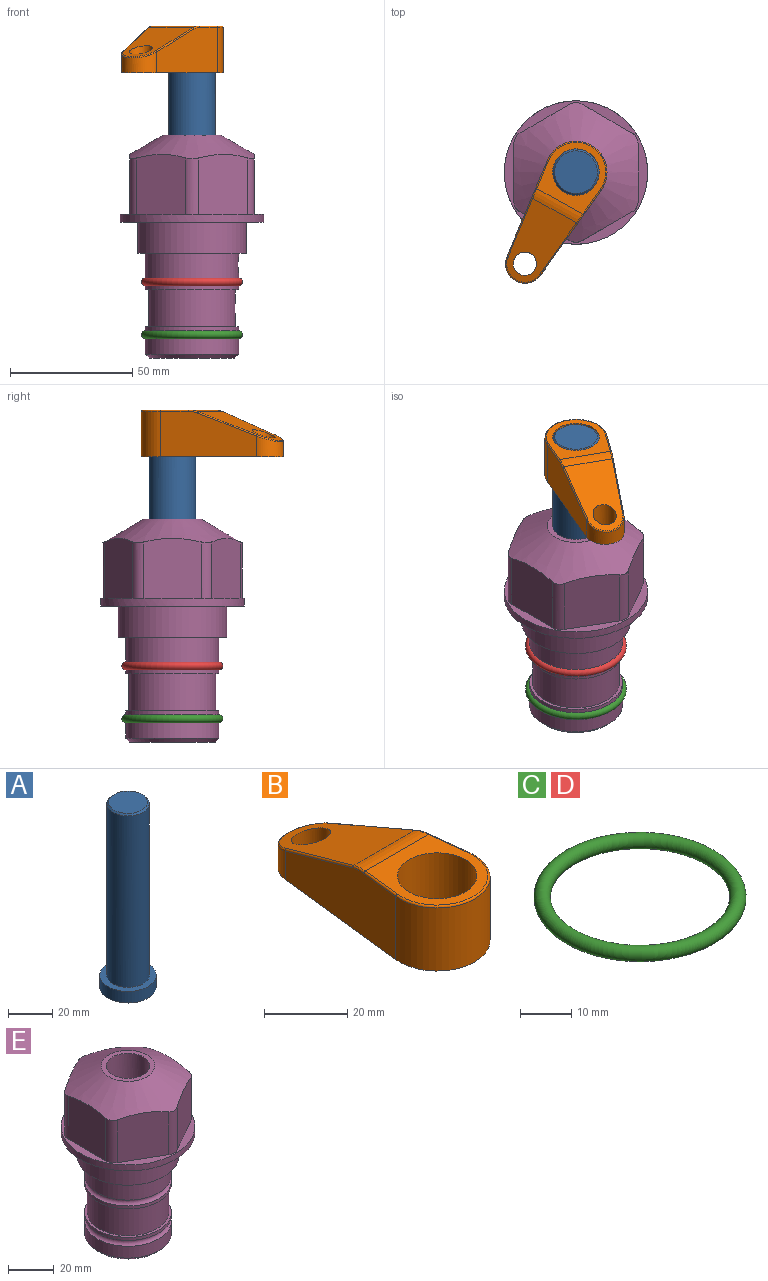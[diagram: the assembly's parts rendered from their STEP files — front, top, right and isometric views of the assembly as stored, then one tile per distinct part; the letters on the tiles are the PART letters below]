
ASSEMBLY  parts=5 mates=3
PART A: 6 faces, bbox 25.4x25.4x101.6 mm
  f0: plane 17.46x17.46mm, normal (0,0,1), area 239.5mm2, adj f5
  f1: plane 25.4x25.4mm, normal (0,0,-1), area 506.7mm2, adj f2
  f2: cylinder r=12.7mm len=25.4mm, axis (0,0,1), area 506.7mm2, adj f1,f3
  f3: plane 25.4x25.4mm, normal (0,0,1), area 221.7mm2, adj f2,f4
  f4: cylinder r=9.53mm len=94.46mm, axis (0,0,1), area 5653mm2, adj f3,f5
  f5: cone r=8.73mm half-angle=45deg, axis (0,0,-1), area 64.4mm2, adj f0,f4
PART B: 44 faces, bbox 27.5x64.5x19.1 mm
  f0: plane 2.3x0.95mm, normal (0,0,-1), area 1mm2, adj f25,f30,f34
  f1: plane 63.5x25.4mm, normal (0,0,-1), area 561.7mm2, adj f2,f3,f4,f5,f6,f7,f19,f20
  f2: cylinder r=12.7mm len=25.4mm, axis (0,0,-1), area 792.2mm2, adj f1,f3,f5,f13
  f3: plane 42.33x18.54mm, normal (0.99,0.11,0), area 647mm2, adj f1,f2,f4,f11,f12,f14
  f4: cylinder r=7.94mm len=15.78mm, axis (0,0,-1), area 158.6mm2, adj f1,f3,f5,f16
  f5: plane 42.33x18.54mm, normal (-0.99,0.11,0), area 647mm2, adj f1,f2,f4,f15,f17,f18
  f6: cylinder r=9.53mm len=19.05mm, axis (0,0,-1), area 1140.1mm2, adj f1,f8
  f7: cylinder r=4.76mm len=10.98mm, axis (0,0,-1), area 276.1mm2, adj f1,f9
  f8: plane 25.83x24.38mm, normal (0,0,1), area 262.2mm2, adj f6,f10,f11,f13,f15
  f9: plane 32.49x20.55mm, normal (0,0.34,0.94), area 489.9mm2, adj f7,f10,f14,f16,f18
  f10: cylinder r=12.7mm len=21.49mm, axis (-1,0,0), area 93.2mm2, adj f8,f9,f12,f17
  f11: cylinder r=0.51mm len=12.34mm, axis (0.11,-0.99,0), area 9.9mm2, adj f3,f8,f12,f13
  f12: bspline ~7.62x1.64mm, area 3.5mm2, adj f3,f10,f11,f14
  f13: torus R=12.19mm, axis (0,0,1), area 33.6mm2, adj f2,f8,f11,f15
  f14: cylinder r=0.51mm len=26.01mm, axis (0.1,-0.93,0.34), area 21.6mm2, adj f3,f9,f12,f16
  f15: cylinder r=0.51mm len=12.34mm, axis (0.11,0.99,0), area 9.9mm2, adj f5,f8,f13,f17
  f16: bspline ~15.78x7.05mm, area 15.7mm2, adj f4,f9,f14,f18
  f17: bspline ~7.62x1.64mm, area 3.5mm2, adj f5,f10,f15,f18
  f18: cylinder r=0.51mm len=26.01mm, axis (0.1,0.93,-0.34), area 21.6mm2, adj f5,f9,f16,f17
  f19: plane 21.6x14.29mm, normal (-0.99,-0.11,0), area 242.6mm2, adj f1,f26,f28,f34,f36,f38
  f20: plane 21.6x14.29mm, normal (0.99,-0.11,0), area 242.6mm2, adj f1,f27,f29,f37,f39,f41
  f21: cylinder r=12.7mm len=14.29mm, axis (0,0,-1), area 173.2mm2, adj f1,f26,f27,f30,f31,f33
  f22: cylinder r=7.94mm len=7.63mm, axis (0,0,-1), area 53.8mm2, adj f1,f28,f29,f42
  f23: plane 2.3x0.95mm, normal (0,0,-1), area 1mm2, adj f25,f33,f37
  f24: plane 17.94x12.32mm, normal (0,-0.34,-0.94), area 191.2mm2, adj f25,f38,f41,f42
  f25: cylinder r=9.53mm len=12.93mm, axis (-1,0,0), area 37.5mm2, adj f0,f23,f24,f31,f36,f39
  f26: cylinder r=1.59mm len=14.29mm, axis (0,0,-1), area 49mm2, adj f1,f19,f21,f32
  f27: cylinder r=1.59mm len=14.29mm, axis (0,0,-1), area 49mm2, adj f1,f20,f21,f35
  f28: cylinder r=1.59mm len=7.28mm, axis (0,0,-1), area 22.1mm2, adj f1,f19,f22,f40
  f29: cylinder r=1.59mm len=7.28mm, axis (0,0,-1), area 22.1mm2, adj f1,f20,f22,f43
  f30: torus R=14.29mm, axis (0,0,1), area 5.8mm2, adj f0,f21,f31,f32
  f31: bspline ~11.06x2.73mm, area 20.8mm2, adj f21,f25,f30,f33
  f32: sphere r=1.59mm, area 5.4mm2, adj f26,f30,f34
  f33: torus R=14.29mm, axis (0,0,1), area 5.8mm2, adj f21,f23,f31,f35
  f34: cylinder r=1.59mm len=1.68mm, axis (-0.11,0.99,0), area 2.4mm2, adj f0,f19,f32,f36
  f35: sphere r=1.59mm, area 5.4mm2, adj f27,f33,f37
  f36: bspline ~5.82x2.33mm, area 7.7mm2, adj f19,f25,f34,f38
  f37: cylinder r=1.59mm len=1.68mm, axis (0.11,0.99,0), area 2.4mm2, adj f20,f23,f35,f39
  f38: cylinder r=1.59mm len=18.33mm, axis (0.1,-0.93,0.34), area 46.7mm2, adj f19,f24,f36,f40
  f39: bspline ~5.82x2.33mm, area 7.7mm2, adj f20,f25,f37,f41
  f40: sphere r=1.59mm, area 3.6mm2, adj f28,f38,f42
  f41: cylinder r=1.59mm len=18.33mm, axis (0.1,0.93,-0.34), area 46.7mm2, adj f20,f24,f39,f43
  f42: bspline ~8.31x1.84mm, area 15.3mm2, adj f22,f24,f40,f43
  f43: sphere r=1.59mm, area 3.6mm2, adj f29,f41,f42
PART C: 1 faces, bbox 44.7x44.7x3.2 mm
  f0: torus R=19.05mm, axis (0,0,1), area 1193.9mm2
PART D: same geometry as C
PART E: 36 faces, bbox 58.7x58.7x91.2 mm
  f0: cylinder r=17.78mm len=35.56mm, axis (0,0,1), area 1670.8mm2, adj f23,f24,f31
  f1: cylinder r=19.05mm len=38.1mm, axis (0,0,1), area 1191.9mm2, adj f26,f27,f30
  f2: plane 58.66x58.66mm, normal (0,0,-1), area 1150.6mm2, adj f3,f28
  f3: cylinder r=29.33mm len=58.66mm, axis (0,0,-1), area 585.1mm2, adj f2,f4
  f4: plane 58.66x58.66mm, normal (0,0,1), area 475.9mm2, adj f3,f5,f6,f7,f8,f9,f10,f11
  f5: plane 24.5x20.32mm, normal (-0.5,0.87,0), area 562.8mm2, adj f4,f15,f16,f17
  f6: plane 24.5x20.32mm, normal (0.5,0.87,0), area 562.8mm2, adj f4,f14,f15,f17
  f7: plane 24.5x23.48mm, normal (1,0,0), area 562.8mm2, adj f4,f13,f14,f17
  f8: plane 24.5x20.32mm, normal (0.5,-0.87,0), area 562.8mm2, adj f4,f12,f13,f17
  f9: plane 24.5x20.32mm, normal (-0.5,-0.87,0), area 562.8mm2, adj f4,f11,f12,f17
  f10: plane 24.5x23.48mm, normal (-1,0,0), area 562.8mm2, adj f4,f11,f16,f17
  f11: cylinder r=5.08mm len=23.01mm, axis (0,0,-1), area 121.2mm2, adj f4,f9,f10,f17
  f12: cylinder r=5.08mm len=23.01mm, axis (0,0,-1), area 121.2mm2, adj f4,f8,f9,f17
  f13: cylinder r=5.08mm len=23.01mm, axis (0,0,-1), area 121.2mm2, adj f4,f7,f8,f17
  f14: cylinder r=5.08mm len=23.01mm, axis (0,0,-1), area 121.2mm2, adj f4,f6,f7,f17
  f15: cylinder r=5.08mm len=23.01mm, axis (0,0,-1), area 121.2mm2, adj f4,f5,f6,f17
  f16: cylinder r=5.08mm len=23.01mm, axis (0,0,-1), area 121.2mm2, adj f4,f5,f10,f17
  f17: cone r=11.73mm half-angle=60deg, axis (0,0,-1), area 2071.8mm2, adj f5,f6,f7,f8,f9,f10,f11,f12
  f18: plane 23.46x23.46mm, normal (0,0,1), area 147.4mm2, adj f17,f35
  f19: plane 34.93x34.93mm, normal (0,0,-1), area 958mm2, adj f29
  f20: cylinder r=19.05mm len=38.1mm, axis (0,0,1), area 760.1mm2, adj f21,f29
  f21: torus R=19.05mm, axis (0,0,1), area 565.3mm2, adj f20,f22
  f22: cylinder r=19.05mm len=38.1mm, axis (0,0,1), area 190mm2, adj f21,f23
  f23: plane 38.1x38.1mm, normal (0,0,1), area 146.9mm2, adj f0,f22
  f24: plane 38.1x38.1mm, normal (0,0,-1), area 146.9mm2, adj f0,f25
  f25: cylinder r=19.05mm len=38.1mm, axis (0,0,1), area 190mm2, adj f24,f26
  f26: torus R=19.05mm, axis (0,0,1), area 565.3mm2, adj f1,f25
  f27: plane 44.45x44.45mm, normal (0,0,-1), area 411.7mm2, adj f1,f28
  f28: cylinder r=22.23mm len=44.45mm, axis (0,0,1), area 1773.5mm2, adj f2,f27
  f29: cone r=19.05mm half-angle=45deg, axis (0,0,1), area 257.5mm2, adj f19,f20
  f30: cylinder r=3.17mm len=6.75mm, axis (-1,0,0), area 128mm2, adj f1,f33
  f31: cylinder r=3.17mm len=6.35mm, axis (-1,0,0), area 102.5mm2, adj f0,f33
  f32: plane 25.4x25.4mm, normal (0,0,1), area 506.7mm2, adj f33
  f33: cylinder r=12.7mm len=66.42mm, axis (0,0,-1), area 5236.2mm2, adj f30,f31,f32,f34
  f34: cone r=9.53mm half-angle=30deg, axis (0,0,-1), area 443.4mm2, adj f33,f35
  f35: cylinder r=9.53mm len=19.05mm, axis (0,0,-1), area 849mm2, adj f18,f34
PLACE A rot(axis=(0,0,-1),119.1deg) t=(0,0,6.51)mm
PLACE B rot(axis=(0,0,1),150.9deg) t=(0,0,61.12)mm
PLACE C t=(0,0,-21.59)mm
PLACE D at identity
PLACE E at identity fixed
MATE fastened C.f0 <-> E.f0  axis (0,0,1) through (0,0,-46.1)mm
MATE cylindrical A.f2 <-> E.f0  axis (0,0,1) through (0,0,32.15)mm
MATE fastened B.f2 <-> A.f2  axis (0,0,1) through (0,0,80.17)mm
